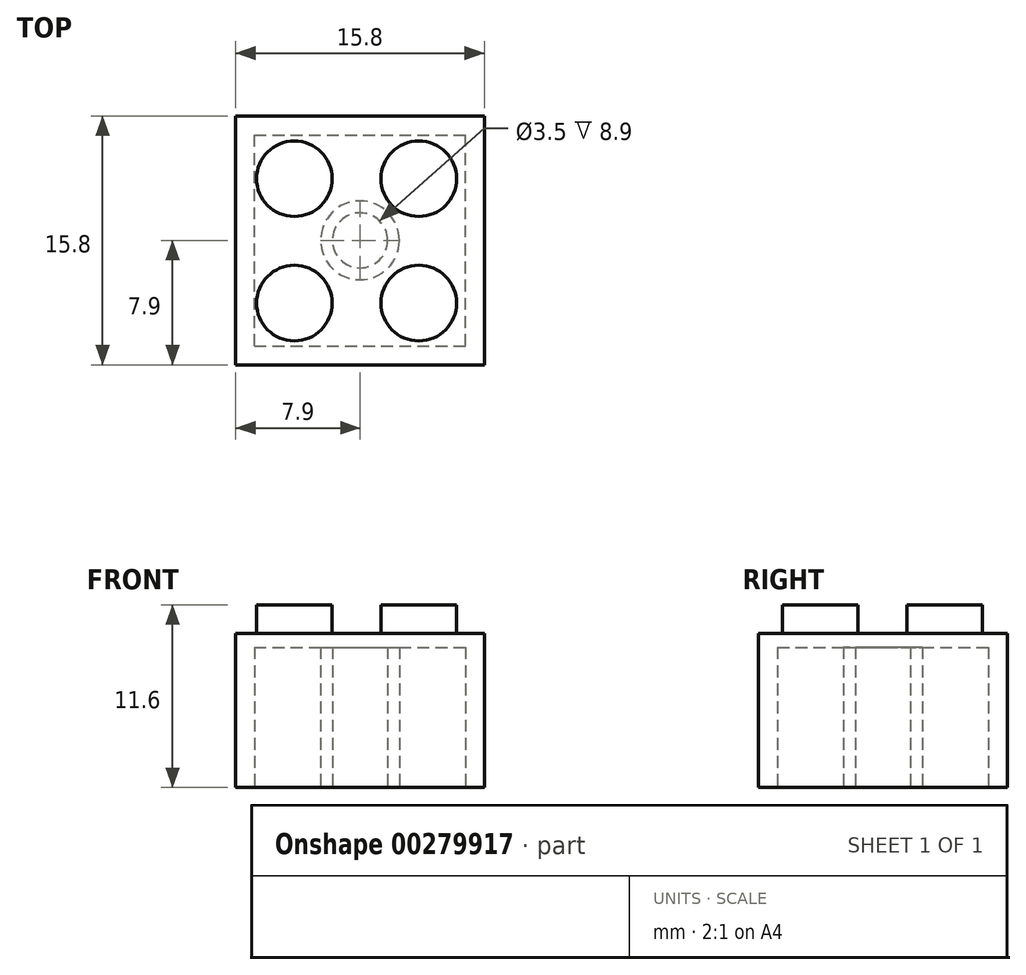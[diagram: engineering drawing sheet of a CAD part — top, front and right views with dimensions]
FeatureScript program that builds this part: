
annotation { "Feature Type Name" : "Feature", "Feature Type Description" : "" }
export const myFeature = defineFeature(function(context is Context, id is Id, definition is map)
    precondition{}
    {
        {
            var Q0;
            Q0=qCreatedBy(makeId("Top.planeOp"),FACE);
            var sketch = newSketch(context, id + "F0", { "sketchPlane" : qUnion([Q0])});
            skLineSegment(sketch, "E0.bottom", {"start": v(-7.9, 7.9) * mm, "end": v(7.9, 7.9) * mm});
            skLineSegment(sketch, "E0.top", {"start": v(-7.9, -7.9) * mm, "end": v(7.9, -7.9) * mm});
            skLineSegment(sketch, "E0.left", {"start": v(-7.9, 7.9) * mm, "end": v(-7.9, -7.9) * mm});
            skLineSegment(sketch, "E0.right", {"start": v(7.9, 7.9) * mm, "end": v(7.9, -7.9) * mm});
            skPoint(sketch, "E0.middle", {"position": v(0, 0) * mm});
            skSolve(sketch);
        }
        {
            var Q0;
            Q0=makeQuery(id+"F0.imprint","IMPRINT",FACE,{"disambiguationData":[TD([[makeQuery(id+"F0.imprint","IMPRINT",EDGE,{"derivedFrom":sQuery(id+"F0.wireOp",EDGE,"E0.bottom")}),-1.0]])]});
            extrude(context, id + "F1", {"entities" : qUnion([Q0]), "depth" : 9.8 * mm, "offsetDistance" : 25 * mm});
        }
        {
            var Q0;
            Q0=makeQuery(id+"F1.opExtrude","CAP_FACE",FACE,{"disambiguationData":[OSD([sQuery(id+"F0.wireOp",EDGE,"E0.bottom"),sQuery(id+"F0.wireOp",EDGE,"E0.top"),sQuery(id+"F0.wireOp",EDGE,"E0.left"),sQuery(id+"F0.wireOp",EDGE,"E0.right")])],"isStart":false});
            var sketch = newSketch(context, id + "F2", { "sketchPlane" : qUnion([Q0])});
            skCircle(sketch, "E1", {"center": v(-4.17, 3.92) * mm, "radius": 2.4 * mm});
            skCircle(sketch, "E2.0.1.0", {"center": v(-4.17, -3.98) * mm, "radius": 2.4 * mm});
            skCircle(sketch, "E2.1.0.0", {"center": v(3.73, 3.92) * mm, "radius": 2.4 * mm});
            skCircle(sketch, "E2.1.1.0", {"center": v(3.73, -3.98) * mm, "radius": 2.4 * mm});
            skLineSegment(sketch, "E2.direction1", {"start": v(-4.17, 3.92) * mm, "end": v(3.73, 3.92) * mm, "construction": true});
            skLineSegment(sketch, "E2.direction2", {"start": v(-4.17, 3.92) * mm, "end": v(-4.17, -3.98) * mm, "construction": true});
            skSolve(sketch);
        }
        {
            var Q0;
            Q0=makeQuery(id+"F2.imprint","IMPRINT",FACE,{"disambiguationData":[TD([[makeQuery(id+"F2.imprint","IMPRINT",EDGE,{"derivedFrom":sQuery(id+"F2.wireOp",EDGE,"E1")}),1.0]])]});
            var Q1;
            Q1=makeQuery(id+"F2.imprint","IMPRINT",FACE,{"disambiguationData":[TD([[makeQuery(id+"F2.imprint","IMPRINT",EDGE,{"derivedFrom":sQuery(id+"F2.wireOp",EDGE,"E2.1.0.0")}),1.0]])]});
            var Q2;
            Q2=makeQuery(id+"F2.imprint","IMPRINT",FACE,{"disambiguationData":[TD([[makeQuery(id+"F2.imprint","IMPRINT",EDGE,{"derivedFrom":sQuery(id+"F2.wireOp",EDGE,"E2.1.1.0")}),1.0]])]});
            var Q3;
            Q3=makeQuery(id+"F2.imprint","IMPRINT",FACE,{"disambiguationData":[TD([[makeQuery(id+"F2.imprint","IMPRINT",EDGE,{"derivedFrom":sQuery(id+"F2.wireOp",EDGE,"E2.0.1.0")}),1.0]])]});
            extrude(context, id + "F3", {"entities" : qUnion([Q0, Q1, Q2, Q3]), "operationType" : NewBodyOperationType.ADD, "depth" : 1.8 * mm, "offsetDistance" : 25 * mm});
        }
        {
            var Q0;
            Q0=makeQuery(id+"F1.opExtrude","CAP_FACE",FACE,{"disambiguationData":[OSD([sQuery(id+"F0.wireOp",EDGE,"E0.bottom"),sQuery(id+"F0.wireOp",EDGE,"E0.top"),sQuery(id+"F0.wireOp",EDGE,"E0.left"),sQuery(id+"F0.wireOp",EDGE,"E0.right")])],"isStart":true});
            var sketch = newSketch(context, id + "F4", { "sketchPlane" : qUnion([Q0])});
            skLineSegment(sketch, "E3.bottom", {"start": v(-6.7, 6.7) * mm, "end": v(6.7, 6.7) * mm});
            skLineSegment(sketch, "E3.top", {"start": v(-6.7, -6.7) * mm, "end": v(6.7, -6.7) * mm});
            skLineSegment(sketch, "E3.left", {"start": v(-6.7, 6.7) * mm, "end": v(-6.7, -6.7) * mm});
            skLineSegment(sketch, "E3.right", {"start": v(6.7, 6.7) * mm, "end": v(6.7, -6.7) * mm});
            skPoint(sketch, "E3.middle", {"position": v(0, 0) * mm});
            skCircle(sketch, "E4", {"center": v(0, 0) * mm, "radius": 2.5 * mm});
            skCircle(sketch, "E5", {"center": v(0, 0) * mm, "radius": 1.75 * mm});
            skSolve(sketch);
        }
        {
            var Q0;
            Q0=makeQuery(id+"F4.imprint","IMPRINT",FACE,{"disambiguationData":[TD([[makeQuery(id+"F4.imprint","IMPRINT",EDGE,{"derivedFrom":sQuery(id+"F4.wireOp",EDGE,"E3.bottom")}),-1.0]])]});
            var Q1;
            Q1=makeQuery(id+"F4.imprint","IMPRINT",FACE,{"disambiguationData":[TD([[makeQuery(id+"F4.imprint","IMPRINT",EDGE,{"derivedFrom":sQuery(id+"F4.wireOp",EDGE,"E5")}),1.0]])]});
            extrude(context, id + "F5", {"entities" : qUnion([Q0, Q1]), "operationType" : NewBodyOperationType.REMOVE, "oppositeDirection" : true, "depth" : 8.9 * mm, "offsetDistance" : 25 * mm});
        }
    });
